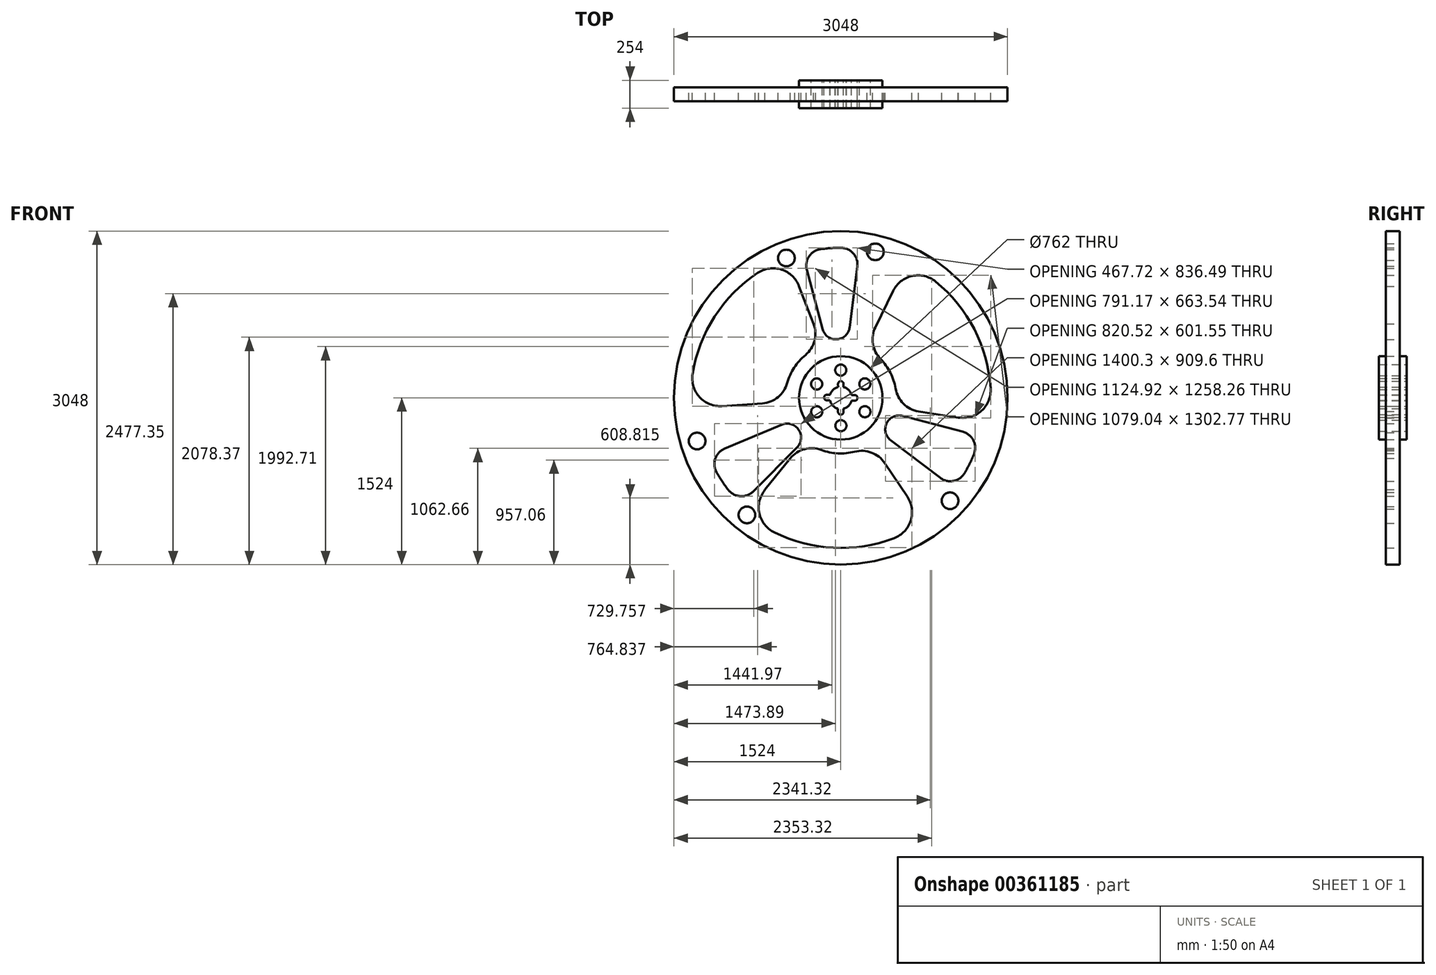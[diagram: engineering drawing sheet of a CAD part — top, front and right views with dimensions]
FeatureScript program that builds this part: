
annotation { "Feature Type Name" : "Feature", "Feature Type Description" : "" }
export const myFeature = defineFeature(function(context is Context, id is Id, definition is map)
    precondition{}
    {
        {
            var Q0;
            Q0=qCreatedBy(makeId("Front.planeOp"),FACE);
            var sketch = newSketch(context, id + "F0", { "sketchPlane" : qUnion([Q0])});
            skCircle(sketch, "E0", {"center": v(0, 0) * mm, "radius": 1524 * mm});
            skArc(sketch, "E1", {"start": v(-759.76, 1141.95) * mm, "mid": v(-1153.17, 742.61) * mm, "end": v(-1353.97, 219.24) * mm});
            skLineSegment(sketch, "E2", {"start": v(-167.36, 629.17) * mm, "end": v(-310.94, 1169) * mm});
            skLineSegment(sketch, "E3", {"start": v(81.38, 645.94) * mm, "end": v(151.2, 1200.15) * mm});
            skArc(sketch, "E4", {"start": v(-184.12, 1359.19) * mm, "mid": v(-290.46, 1292.71) * mm, "end": v(-310.94, 1169) * mm});
            skArc(sketch, "E5", {"start": v(-167.36, 629.17) * mm, "mid": v(-36.08, 535.1) * mm, "end": v(81.38, 645.94) * mm});
            skArc(sketch, "E6.trimOffspring", {"start": v(0, 1371.6) * mm, "mid": v(-92.27, 1368.5) * mm, "end": v(-184.12, 1359.19) * mm});
            skArc(sketch, "E7", {"start": v(500.92, 84.52) * mm, "mid": v(452.54, 230.8) * mm, "end": v(362.53, 355.86) * mm});
            skArc(sketch, "E8", {"start": v(-177.26, -476.07) * mm, "mid": v(-331.8, -468.8) * mm, "end": v(-461.89, -552.54) * mm});
            skArc(sketch, "E9", {"start": v(401.1, -596.03) * mm, "mid": v(280.56, -500.38) * mm, "end": v(126.92, -491.9) * mm});
            skArc(sketch, "E10", {"start": v(487.12, -1282.19) * mm, "mid": v(638.98, -1121.67) * mm, "end": v(607.64, -902.93) * mm});
            skArc(sketch, "E11.1.2", {"start": v(-1130.48, -689.1) * mm, "mid": v(-1071.95, -778.38) * mm, "end": v(-1006.53, -862.75) * mm});
            skLineSegment(sketch, "E12.trimOffspring", {"start": v(401.1, -596.03) * mm, "end": v(607.64, -902.93) * mm});
            skLineSegment(sketch, "E13.trimOffspring", {"start": v(-461.89, -552.54) * mm, "end": v(-692.28, -839.8) * mm});
            skArc(sketch, "E14.trimOffspring", {"start": v(-177.26, -476.07) * mm, "mid": v(-26.39, -507.31) * mm, "end": v(126.92, -491.9) * mm});
            skArc(sketch, "E15.trimOffspring", {"start": v(-609.08, -1228.95) * mm, "mid": v(-66.54, -1369.99) * mm, "end": v(487.12, -1282.19) * mm});
            skArc(sketch, "E16", {"start": v(151.2, 1200.15) * mm, "mid": v(114.3, 1320) * mm, "end": v(0, 1371.6) * mm});
            skPoint(sketch, "E17.orphan", {"position": v(103.3, 1367.7) * mm});
            skArc(sketch, "E18.1.0", {"start": v(-1135.09, -681.63) * mm, "mid": v(-1084.3, -762.9) * mm, "end": v(-1027.96, -840.42) * mm});
            skArc(sketch, "E18.1.1", {"start": v(-1027.96, -840.42) * mm, "mid": v(-916.93, -898.7) * mm, "end": v(-799.77, -853.99) * mm});
            skLineSegment(sketch, "E18.1.2", {"start": v(-399.91, -451.49) * mm, "end": v(-799.77, -853.99) * mm});
            skArc(sketch, "E18.1.3", {"start": v(-399.91, -451.49) * mm, "mid": v(-384.73, -290.96) * mm, "end": v(-539.27, -244.92) * mm});
            skLineSegment(sketch, "E18.1.4", {"start": v(-539.27, -244.92) * mm, "end": v(-1062.21, -464.95) * mm});
            skArc(sketch, "E18.1.5", {"start": v(-1062.21, -464.95) * mm, "mid": v(-1147.55, -556.84) * mm, "end": v(-1135.09, -681.63) * mm});
            skArc(sketch, "E18.2.0", {"start": v(1132.66, -685.93) * mm, "mid": v(1177.65, -601.31) * mm, "end": v(1216.62, -513.76) * mm});
            skArc(sketch, "E18.2.1", {"start": v(1216.62, -513.76) * mm, "mid": v(1211.58, -388.46) * mm, "end": v(1114.26, -309.35) * mm});
            skLineSegment(sketch, "E18.2.2", {"start": v(565.77, -164.32) * mm, "end": v(1114.26, -309.35) * mm});
            skArc(sketch, "E18.2.3", {"start": v(565.77, -164.32) * mm, "mid": v(419.15, -231.44) * mm, "end": v(456.55, -388.29) * mm});
            skLineSegment(sketch, "E18.2.4", {"start": v(456.55, -388.29) * mm, "end": v(908.58, -731.15) * mm});
            skArc(sketch, "E18.2.5", {"start": v(908.58, -731.15) * mm, "mid": v(1030.83, -759.12) * mm, "end": v(1132.66, -685.93) * mm});
            skPoint(sketch, "E19.orphan", {"position": v(-405.66, -499.28) * mm});
            skArc(sketch, "E20", {"start": v(-692.28, -839.8) * mm, "mid": v(-744.67, -1054.47) * mm, "end": v(-609.08, -1228.95) * mm});
            skArc(sketch, "E21.1.0", {"start": v(1073.43, -179.63) * mm, "mid": v(1285.53, -117.67) * mm, "end": v(1368.84, 87) * mm});
            skArc(sketch, "E21.1.1", {"start": v(1368.84, 87) * mm, "mid": v(1219.71, 627.37) * mm, "end": v(866.85, 1062.95) * mm});
            skArc(sketch, "E21.1.2", {"start": v(866.85, 1062.95) * mm, "mid": v(651.9, 1114.21) * mm, "end": v(478.14, 977.7) * mm});
            skLineSegment(sketch, "E21.1.3", {"start": v(315.62, 645.38) * mm, "end": v(478.14, 977.7) * mm});
            skArc(sketch, "E21.1.4", {"start": v(315.62, 645.38) * mm, "mid": v(293.07, 493.16) * mm, "end": v(362.53, 355.86) * mm});
            skArc(sketch, "E21.1.6", {"start": v(500.92, 84.52) * mm, "mid": v(571.9, -52.94) * mm, "end": v(709.46, -123.73) * mm});
            skArc(sketch, "E21.2.0", {"start": v(-381.15, 1019.43) * mm, "mid": v(-540.86, 1172.14) * mm, "end": v(-759.76, 1141.95) * mm});
            skArc(sketch, "E21.2.2", {"start": v(-1353.97, 219.24) * mm, "mid": v(-1290.89, 7.46) * mm, "end": v(-1085.78, -74.76) * mm});
            skLineSegment(sketch, "E21.2.3", {"start": v(-716.72, -49.35) * mm, "end": v(-1085.78, -74.76) * mm});
            skArc(sketch, "E21.2.4", {"start": v(-716.72, -49.35) * mm, "mid": v(-573.62, 7.22) * mm, "end": v(-489.45, 136.03) * mm});
            skArc(sketch, "E21.2.5", {"start": v(-323.66, 391.55) * mm, "mid": v(-426.15, 276.5) * mm, "end": v(-489.45, 136.03) * mm});
            skArc(sketch, "E21.2.6", {"start": v(-323.66, 391.55) * mm, "mid": v(-240.1, 521.75) * mm, "end": v(-247.57, 676.27) * mm});
            skLineSegment(sketch, "E21.2.7", {"start": v(-247.57, 676.27) * mm, "end": v(-381.15, 1019.43) * mm});
            skCircle(sketch, "E22", {"center": v(-497.6, 1278.16) * mm, "radius": 76.2 * mm});
            skCircle(sketch, "E23", {"center": v(315.2, 1334.9) * mm, "radius": 76.2 * mm});
            skCircle(sketch, "E24.1.0", {"center": v(-858.12, -1070.01) * mm, "radius": 76.2 * mm});
            skCircle(sketch, "E24.1.1", {"center": v(-1313.65, -394.47) * mm, "radius": 76.2 * mm});
            skCircle(sketch, "E24.2.1", {"center": v(998.45, -940.42) * mm, "radius": 76.2 * mm});
            skPoint(sketch, "E25.orphan", {"position": v(-954.27, -921.31) * mm});
            skPoint(sketch, "E26.orphan", {"position": v(-1189.52, -579.54) * mm});
            skLineSegment(sketch, "E27", {"start": v(709.46, -123.73) * mm, "end": v(1073.43, -179.63) * mm});
            skCircle(sketch, "E28", {"center": v(0, 0) * mm, "radius": 381 * mm});
            skArc(sketch, "E29", {"start": v(-24.27, 98.66) * mm, "mid": v(-70.27, 73.38) * mm, "end": v(-97.52, 28.51) * mm});
            skArc(sketch, "E30", {"start": v(25.4, 127) * mm, "mid": v(-0.52, 152.4) * mm, "end": v(-25.38, 125.97) * mm});
            skArc(sketch, "E31", {"start": v(-25.4, -127) * mm, "mid": v(0, -152.4) * mm, "end": v(25.4, -127) * mm});
            skArc(sketch, "E32", {"start": v(-126.96, 28.51) * mm, "mid": v(-152.36, 3.38) * mm, "end": v(-127.5, -22.28) * mm});
            skArc(sketch, "E33", {"start": v(127, -25.53) * mm, "mid": v(152.4, -0.13) * mm, "end": v(127, 25.27) * mm});
            skLineSegment(sketch, "E34", {"start": v(25.4, 127) * mm, "end": v(25.4, 98.37) * mm});
            skLineSegment(sketch, "E35", {"start": v(-25.38, 125.97) * mm, "end": v(-24.27, 98.66) * mm});
            skLineSegment(sketch, "E36", {"start": v(-126.96, 28.51) * mm, "end": v(-97.52, 28.51) * mm});
            skLineSegment(sketch, "E37", {"start": v(-127.5, -22.28) * mm, "end": v(-98.99, -22.88) * mm});
            skLineSegment(sketch, "E38", {"start": v(25.4, -127) * mm, "end": v(25.4, -98.37) * mm});
            skLineSegment(sketch, "E39", {"start": v(-25.4, -127) * mm, "end": v(-25.4, -98.37) * mm});
            skLineSegment(sketch, "E40", {"start": v(127, -25.53) * mm, "end": v(98.34, -25.53) * mm});
            skLineSegment(sketch, "E41", {"start": v(127, 25.27) * mm, "end": v(98.4, 25.27) * mm});
            skArc(sketch, "E42.trimOffspring", {"start": v(98.4, 25.27) * mm, "mid": v(71.9, 71.8) * mm, "end": v(25.4, 98.37) * mm});
            skArc(sketch, "E43.trimOffspring", {"start": v(25.4, -98.37) * mm, "mid": v(71.8, -71.9) * mm, "end": v(98.34, -25.53) * mm});
            skArc(sketch, "E44.trimOffspring", {"start": v(-98.99, -22.88) * mm, "mid": v(-72.75, -70.92) * mm, "end": v(-25.4, -98.37) * mm});
            skCircle(sketch, "E45", {"center": v(-0.52, 254) * mm, "radius": 50.8 * mm});
            skPoint(sketch, "E45.centerSnap0", {"position": v(-0.52, 152.4) * mm});
            skCircle(sketch, "E46.1.0", {"center": v(-220.23, 126.55) * mm, "radius": 50.8 * mm});
            skCircle(sketch, "E46.2.0", {"center": v(-219.71, -127.45) * mm, "radius": 50.8 * mm});
            skCircle(sketch, "E46.3.0", {"center": v(0.52, -254) * mm, "radius": 50.8 * mm});
            skCircle(sketch, "E46.4.0", {"center": v(220.23, -126.55) * mm, "radius": 50.8 * mm});
            skCircle(sketch, "E46.5.0", {"center": v(219.71, 127.45) * mm, "radius": 50.8 * mm});
            skSolve(sketch);
        }
        {
            var Q0;
            Q0=makeQuery(id+"F0.imprint","IMPRINT",FACE,{"disambiguationData":[TD([[makeQuery(id+"F0.imprint","IMPRINT",EDGE,{"derivedFrom":sQuery(id+"F0.wireOp",EDGE,"E0")}),1.0]])]});
            extrude(context, id + "F1", {"entities" : qUnion([Q0]), "depth" : 127 * mm, "symmetric" : true});
        }
        {
            var Q0;
            Q0=makeQuery(id+"F0.imprint","IMPRINT",FACE,{"disambiguationData":[TD([[makeQuery(id+"F0.imprint","IMPRINT",EDGE,{"derivedFrom":sQuery(id+"F0.wireOp",EDGE,"E28")}),1.0]])]});
            extrude(context, id + "F2", {"entities" : qUnion([Q0]), "depth" : 254 * mm, "symmetric" : true});
        }
    });
